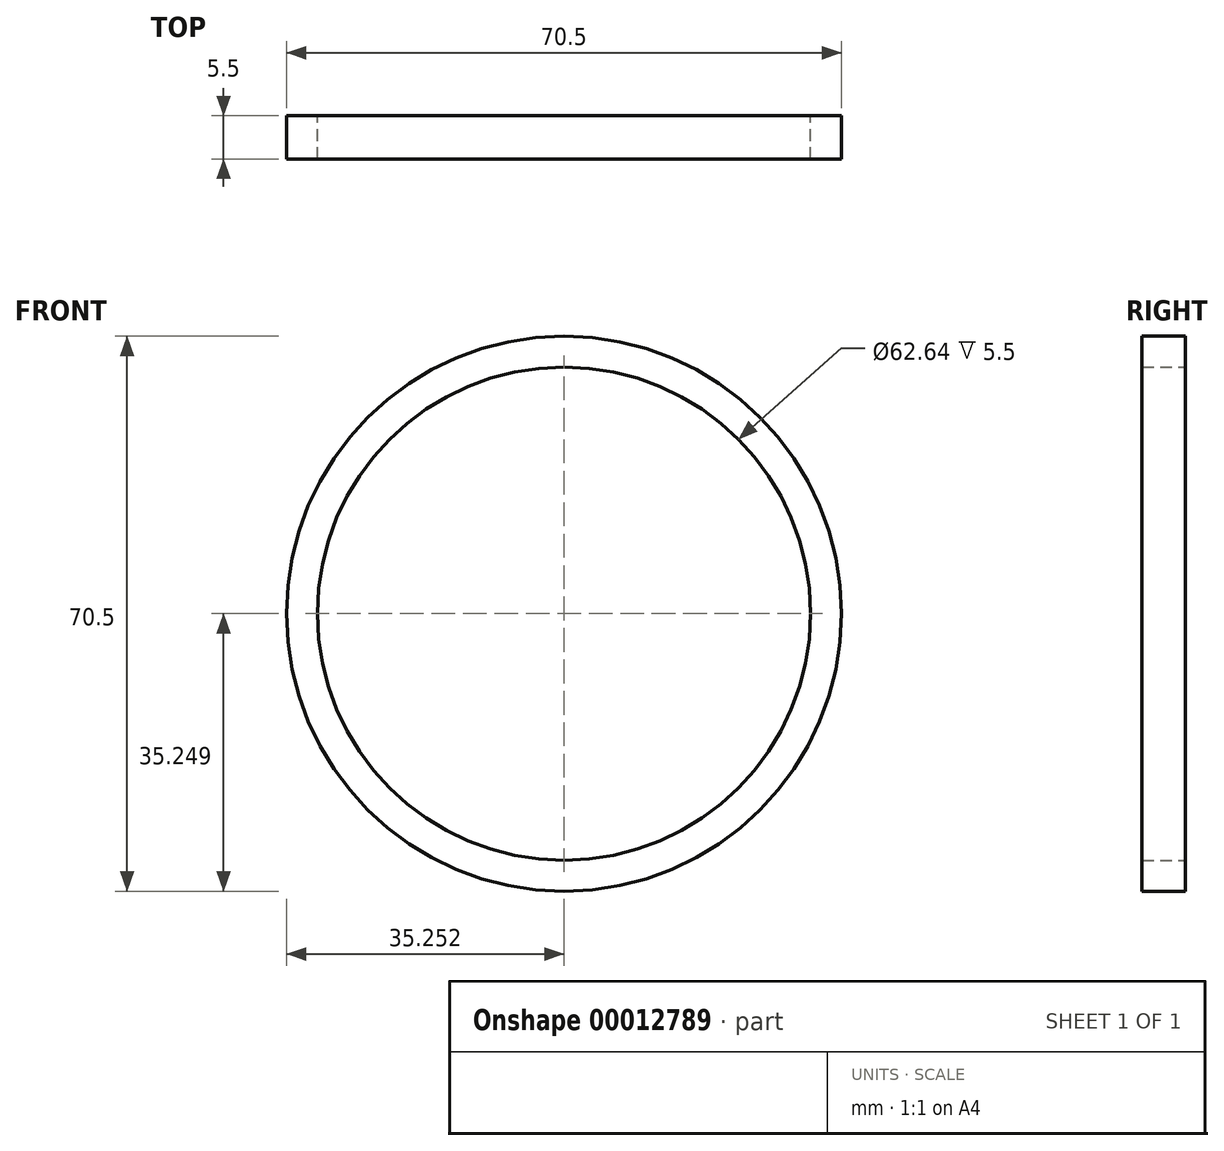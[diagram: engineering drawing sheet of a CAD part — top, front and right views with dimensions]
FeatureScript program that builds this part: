
annotation { "Feature Type Name" : "Feature", "Feature Type Description" : "" }
export const myFeature = defineFeature(function(context is Context, id is Id, definition is map)
    precondition{}
    {
        {
            var Q0;
            Q0=qCreatedBy(makeId("Front.planeOp"),FACE);
            var sketch = newSketch(context, id + "F0", { "sketchPlane" : qUnion([Q0])});
            skCircle(sketch, "E0", {"center": v(-31.65, 38.28) * mm, "radius": 35.25 * mm});
            skCircle(sketch, "E1", {"center": v(-31.65, 38.28) * mm, "radius": 31.32 * mm});
            skSolve(sketch);
        }
        {
            var Q0;
            Q0=makeQuery(id+"F0.imprint","IMPRINT",FACE,{"disambiguationData":[TD([[makeQuery(id+"F0.imprint","IMPRINT",EDGE,{"derivedFrom":sQuery(id+"F0.wireOp",EDGE,"E0")}),1.0]])]});
            extrude(context, id + "F1", {"entities" : qUnion([Q0]), "depth" : 5.5 * mm});
        }
    });
